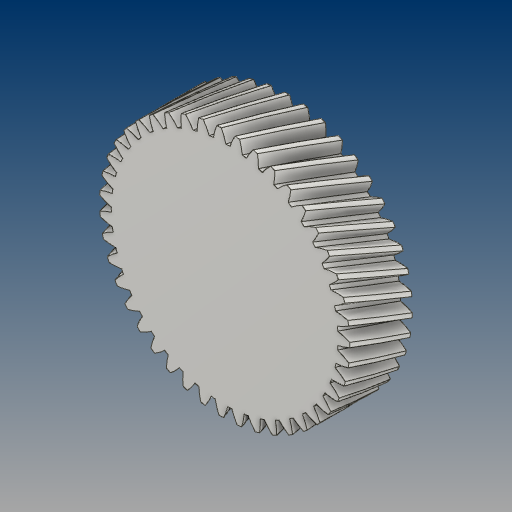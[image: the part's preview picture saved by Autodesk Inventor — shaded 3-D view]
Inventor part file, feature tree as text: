
AUTODESK INVENTOR PART (.ipt)
format: ipt  version: 2021 (Build 250183000, 183)  size: 718,848 bytes
history: native  units: mm (DEFAULTED — no unit token found)
features: plane x3, other x3, sketch x2, extrude x1
ambient origin geometry x8: Origin, YZ Plane, XZ Plane, XY Plane, X Axis, Y Axis, Z Axis, Center Point
bodies: Solid1 (feature_tree)
feature tree (9):
  extrude  "Extrusion1"  Depth=15.0mm TaperAngle=0.0deg
  plane  "Work Plane2"
  plane  "Work Plane8"
  plane  "Work Plane9"
  other  "Spur Gear"
  sketch  "Sketch1"  dims[d0=59.886222mm d1=15.0mm d2=0.0mm]
  sketch  "Sketch2"  dims[d3=57.199555mm d4=10.0mm d5=0.0mm d16=40.0mm d17=0.0mm d34=0.730603mm d39=0.0mm d41=0.0mm d43=40.0mm d46=40.0mm d47=0.0mm d48=0.0mm]
  other  "Srf1"
  other  "Pitch Diameter"
